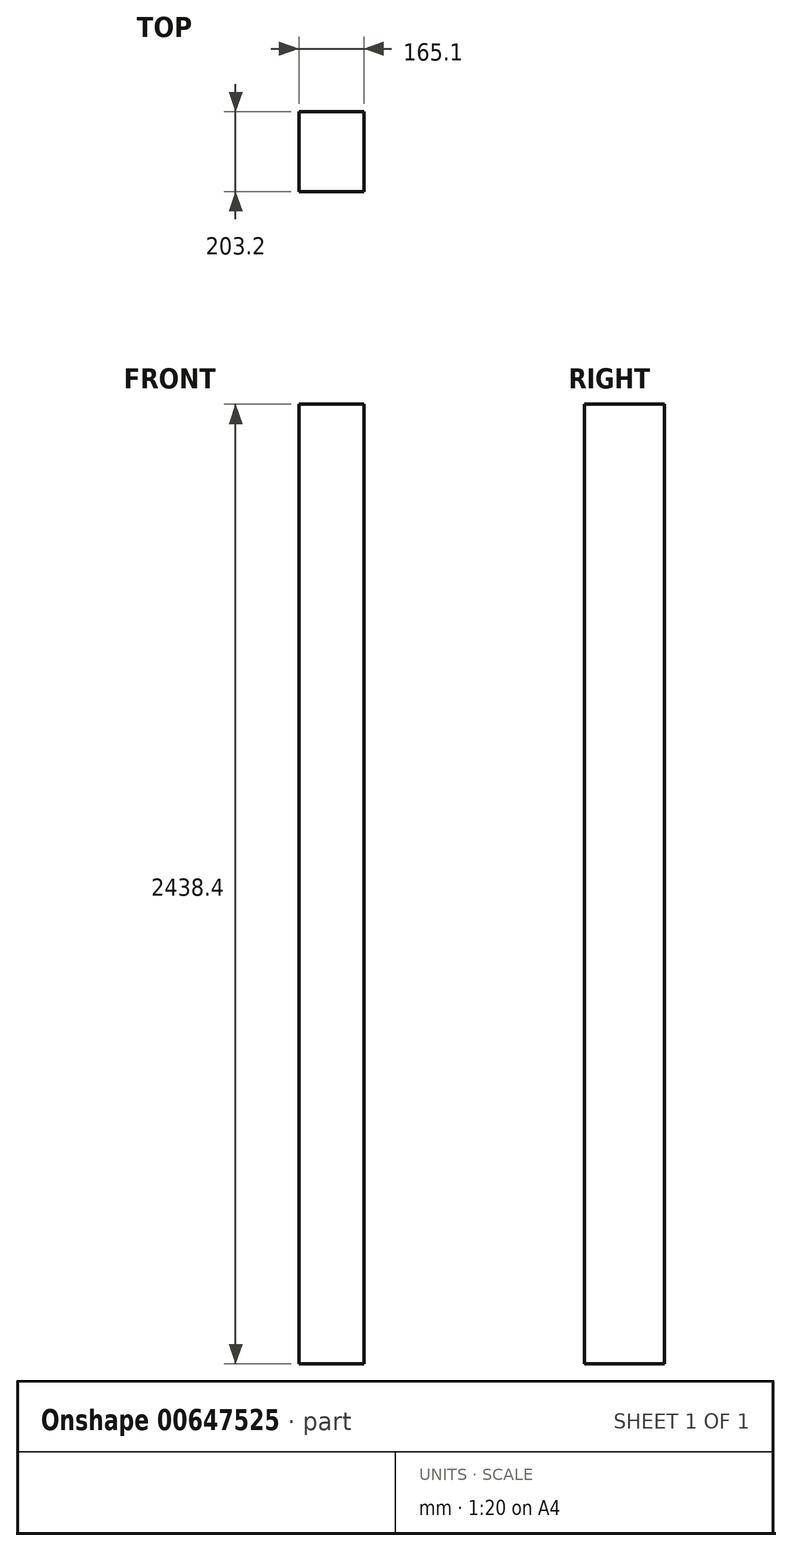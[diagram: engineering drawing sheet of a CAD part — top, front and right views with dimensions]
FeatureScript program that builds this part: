
annotation { "Feature Type Name" : "Feature", "Feature Type Description" : "" }
export const myFeature = defineFeature(function(context is Context, id is Id, definition is map)
    precondition{}
    {
        {
            var Q0;
            Q0=qCreatedBy(makeId("Top.planeOp"),FACE);
            var sketch = newSketch(context, id + "F0", { "sketchPlane" : qUnion([Q0])});
            skLineSegment(sketch, "E0.bottom", {"start": v(82.55, -101.6) * mm, "end": v(-82.55, -101.6) * mm});
            skLineSegment(sketch, "E0.top", {"start": v(82.55, 101.6) * mm, "end": v(-82.55, 101.6) * mm});
            skLineSegment(sketch, "E0.left", {"start": v(82.55, -101.6) * mm, "end": v(82.55, 101.6) * mm});
            skLineSegment(sketch, "E0.right", {"start": v(-82.55, -101.6) * mm, "end": v(-82.55, 101.6) * mm});
            skPoint(sketch, "E0.middle", {"position": v(0, 0) * mm});
            skSolve(sketch);
        }
        {
            var Q0;
            Q0=makeQuery(id+"F0.imprint","IMPRINT",FACE,{"disambiguationData":[TD([[makeQuery(id+"F0.imprint","IMPRINT",EDGE,{"derivedFrom":sQuery(id+"F0.wireOp",EDGE,"E0.bottom")}),-1.0]])]});
            extrude(context, id + "F1", {"entities" : qUnion([Q0]), "depth" : 2438.4 * mm, "offsetDistance" : 25.4 * mm});
        }
    });
